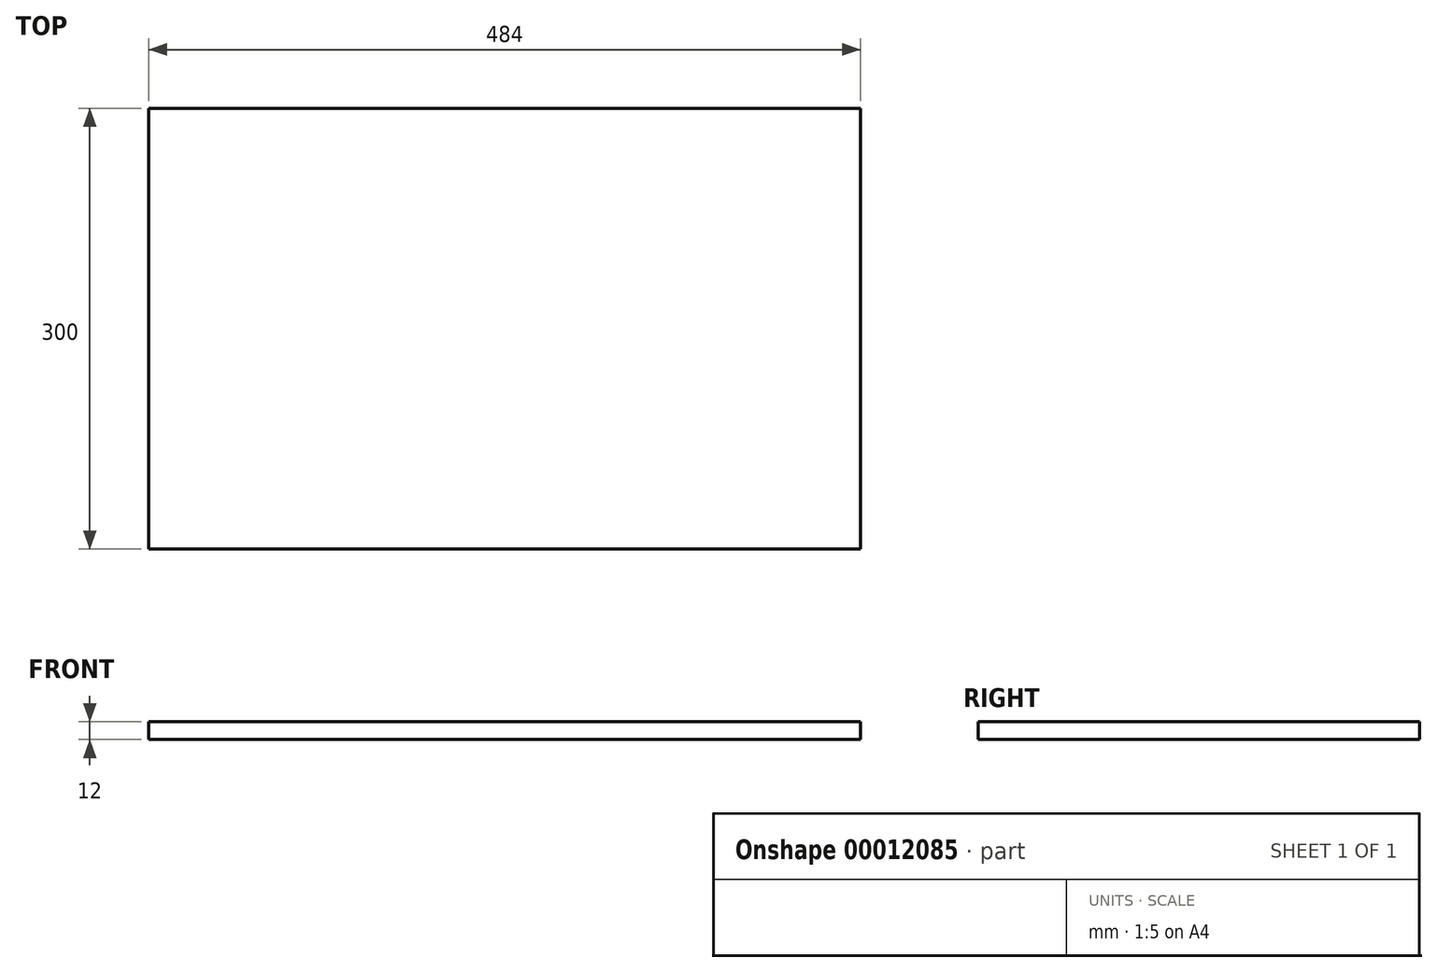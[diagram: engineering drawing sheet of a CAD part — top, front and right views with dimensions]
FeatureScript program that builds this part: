
annotation { "Feature Type Name" : "Feature", "Feature Type Description" : "" }
export const myFeature = defineFeature(function(context is Context, id is Id, definition is map)
    precondition{}
    {
        {
            var Q0;
            Q0=qCreatedBy(makeId("Top.planeOp"),FACE);
            var sketch = newSketch(context, id + "F0", { "sketchPlane" : qUnion([Q0])});
            skLineSegment(sketch, "E0.bottom", {"start": v(0, 0) * mm, "end": v(484, 0) * mm});
            skLineSegment(sketch, "E0.top", {"start": v(0, 300) * mm, "end": v(484, 300) * mm});
            skLineSegment(sketch, "E0.left", {"start": v(0, 0) * mm, "end": v(0, 300) * mm});
            skLineSegment(sketch, "E0.right", {"start": v(484, 0) * mm, "end": v(484, 300) * mm});
            skSolve(sketch);
        }
        {
            var Q0;
            Q0 = qSketchRegion(id + "F0", true);
            extrude(context, id + "F1", {"entities" : qUnion([Q0]), "depth" : 12 * mm});
        }
    });
